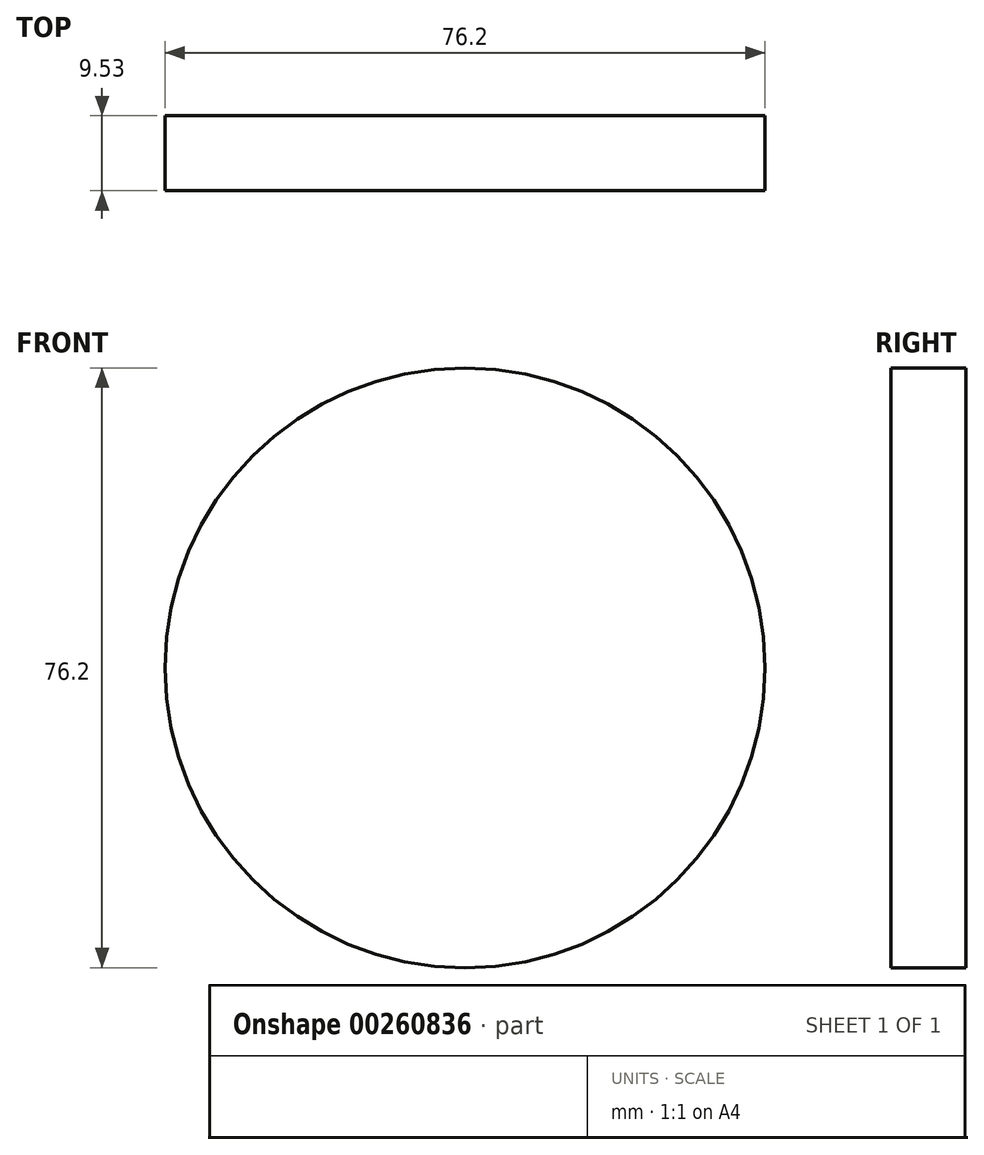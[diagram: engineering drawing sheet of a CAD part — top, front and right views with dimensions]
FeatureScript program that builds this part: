
annotation { "Feature Type Name" : "Feature", "Feature Type Description" : "" }
export const myFeature = defineFeature(function(context is Context, id is Id, definition is map)
    precondition{}
    {
        {
            var Q0;
            Q0=qCreatedBy(makeId("Front.planeOp"),FACE);
            var sketch = newSketch(context, id + "F0", { "sketchPlane" : qUnion([Q0])});
            skCircle(sketch, "E0", {"center": v(0, 0) * mm, "radius": 38.1 * mm});
            skSolve(sketch);
        }
        {
            var Q0;
            Q0 = qSketchRegion(id + "F0", true);
            extrude(context, id + "F1", {"entities" : qUnion([Q0]), "depth" : 9.52 * mm});
        }
    });
